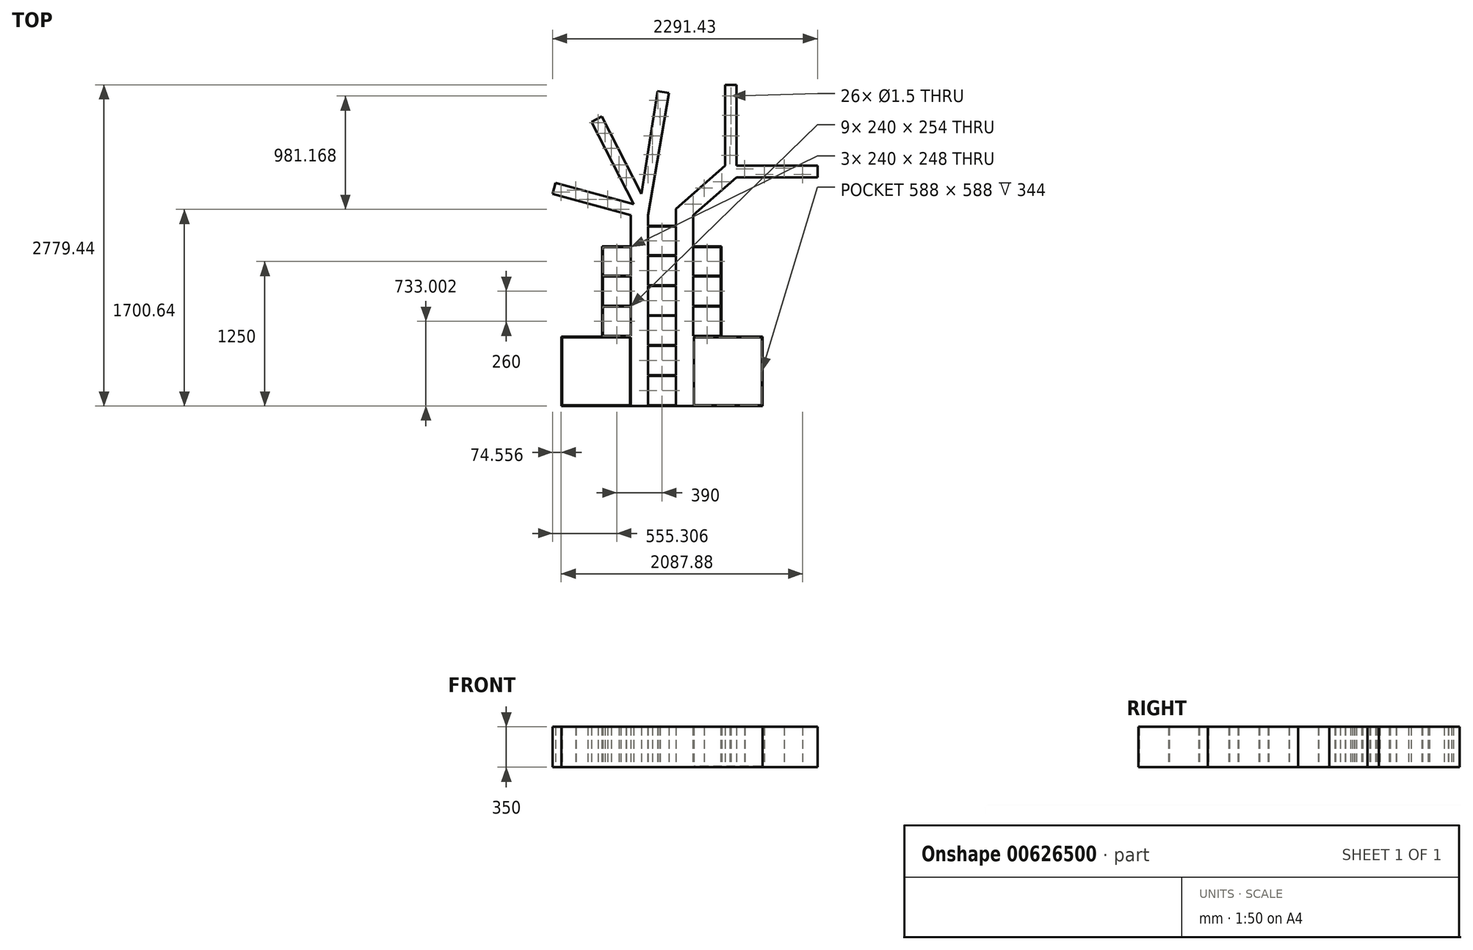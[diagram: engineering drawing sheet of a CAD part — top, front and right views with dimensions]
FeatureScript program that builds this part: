
annotation { "Feature Type Name" : "Feature", "Feature Type Description" : "" }
export const myFeature = defineFeature(function(context is Context, id is Id, definition is map)
    precondition{}
    {
        {
            var Q0;
            Q0=qCreatedBy(makeId("Top.planeOp"),FACE);
            var sketch = newSketch(context, id + "F0", { "sketchPlane" : qUnion([Q0])});
            skLineSegment(sketch, "E0", {"start": v(291.37, -157.74) * mm, "end": v(291.37, 1492.26) * mm});
            skLineSegment(sketch, "E1", {"start": v(831.37, 1492.26) * mm, "end": v(831.37, -157.74) * mm});
            skLineSegment(sketch, "E2", {"start": v(831.37, -157.74) * mm, "end": v(1431.37, -157.74) * mm});
            skLineSegment(sketch, "E3", {"start": v(1431.37, -157.74) * mm, "end": v(1431.37, 442.26) * mm});
            skLineSegment(sketch, "E4", {"start": v(1431.37, 442.26) * mm, "end": v(831.37, 442.26) * mm});
            skLineSegment(sketch, "E5", {"start": v(291.37, -157.74) * mm, "end": v(-308.63, -157.74) * mm});
            skLineSegment(sketch, "E6", {"start": v(-308.63, -157.74) * mm, "end": v(-308.63, 442.26) * mm});
            skLineSegment(sketch, "E7", {"start": v(-308.63, 442.26) * mm, "end": v(291.37, 442.26) * mm});
            skLineSegment(sketch, "E8", {"start": v(831.37, 1492.26) * mm, "end": v(1207.49, 1821.7) * mm});
            skLineSegment(sketch, "E9", {"start": v(1207.49, 1821.7) * mm, "end": v(1907.49, 1821.7) * mm});
            skLineSegment(sketch, "E10", {"start": v(1907.49, 1821.7) * mm, "end": v(1907.49, 1921.7) * mm});
            skLineSegment(sketch, "E11", {"start": v(1907.49, 1921.7) * mm, "end": v(1207.49, 1921.7) * mm});
            skLineSegment(sketch, "E12", {"start": v(1207.49, 1921.7) * mm, "end": v(1207.49, 2621.7) * mm});
            skLineSegment(sketch, "E13", {"start": v(1207.49, 2621.7) * mm, "end": v(1107.49, 2621.7) * mm});
            skLineSegment(sketch, "E14", {"start": v(1107.49, 2621.7) * mm, "end": v(1107.49, 1921.7) * mm});
            skLineSegment(sketch, "E15", {"start": v(291.37, -157.74) * mm, "end": v(441.37, -157.74) * mm});
            skLineSegment(sketch, "E16", {"start": v(441.37, -157.74) * mm, "end": v(681.37, -157.74) * mm});
            skLineSegment(sketch, "E17", {"start": v(681.37, -157.74) * mm, "end": v(831.37, -157.74) * mm});
            skLineSegment(sketch, "E18", {"start": v(681.37, -157.74) * mm, "end": v(681.37, 7.26) * mm});
            skLineSegment(sketch, "E19", {"start": v(681.37, 7.26) * mm, "end": v(681.37, 1492.26) * mm});
            skLineSegment(sketch, "E20", {"start": v(681.37, 1492.26) * mm, "end": v(831.37, 1492.26) * mm});
            skLineSegment(sketch, "E21", {"start": v(441.37, -157.74) * mm, "end": v(441.37, 1492.26) * mm});
            skLineSegment(sketch, "E22", {"start": v(441.37, 1492.26) * mm, "end": v(291.37, 1492.26) * mm});
            skLineSegment(sketch, "E23", {"start": v(1107.49, 1921.7) * mm, "end": v(681.37, 1548.47) * mm});
            skLineSegment(sketch, "E24", {"start": v(681.37, 1548.47) * mm, "end": v(681.37, 1492.26) * mm});
            skLineSegment(sketch, "E25", {"start": v(291.37, 1492.26) * mm, "end": v(-383.94, 1676.57) * mm});
            skLineSegment(sketch, "E26", {"start": v(-383.94, 1676.57) * mm, "end": v(-357.6, 1773.04) * mm});
            skLineSegment(sketch, "E27", {"start": v(-357.6, 1773.04) * mm, "end": v(317.7, 1588.73) * mm});
            skLineSegment(sketch, "E28", {"start": v(317.7, 1588.73) * mm, "end": v(-46.46, 2301.05) * mm});
            skLineSegment(sketch, "E29", {"start": v(-46.46, 2301.05) * mm, "end": v(42.58, 2346.57) * mm});
            skLineSegment(sketch, "E30", {"start": v(42.58, 2346.57) * mm, "end": v(385.1, 1676.57) * mm});
            skLineSegment(sketch, "E31", {"start": v(385.1, 1676.57) * mm, "end": v(523.43, 2565.87) * mm});
            skLineSegment(sketch, "E32", {"start": v(523.43, 2565.87) * mm, "end": v(622.24, 2550.5) * mm});
            skLineSegment(sketch, "E33", {"start": v(622.24, 2550.5) * mm, "end": v(441.37, 1492.26) * mm});
            skLineSegment(sketch, "E34", {"start": v(1071.37, 442.26) * mm, "end": v(831.37, 442.26) * mm});
            skLineSegment(sketch, "E35", {"start": v(1071.37, 442.26) * mm, "end": v(1071.37, 702.26) * mm});
            skLineSegment(sketch, "E36", {"start": v(1071.37, 702.26) * mm, "end": v(831.37, 702.26) * mm});
            skLineSegment(sketch, "E37", {"start": v(1071.37, 702.26) * mm, "end": v(1071.37, 962.26) * mm});
            skLineSegment(sketch, "E38", {"start": v(1071.37, 962.26) * mm, "end": v(831.37, 962.26) * mm});
            skLineSegment(sketch, "E39", {"start": v(1071.37, 962.26) * mm, "end": v(1071.37, 1222.26) * mm});
            skLineSegment(sketch, "E40", {"start": v(1071.37, 1222.26) * mm, "end": v(831.37, 1222.26) * mm});
            skLineSegment(sketch, "E41", {"start": v(51.37, 442.26) * mm, "end": v(291.37, 442.26) * mm});
            skLineSegment(sketch, "E42", {"start": v(51.37, 442.26) * mm, "end": v(51.37, 702.26) * mm});
            skLineSegment(sketch, "E43", {"start": v(51.37, 702.26) * mm, "end": v(291.37, 702.26) * mm});
            skLineSegment(sketch, "E44", {"start": v(51.37, 702.26) * mm, "end": v(51.37, 962.26) * mm});
            skLineSegment(sketch, "E45", {"start": v(291.37, 962.26) * mm, "end": v(51.37, 962.26) * mm});
            skLineSegment(sketch, "E46", {"start": v(51.37, 962.26) * mm, "end": v(51.37, 1222.26) * mm});
            skLineSegment(sketch, "E47", {"start": v(51.37, 1222.26) * mm, "end": v(291.37, 1222.26) * mm});
            skLineSegment(sketch, "E48", {"start": v(441.37, 102.26) * mm, "end": v(441.37, -157.74) * mm});
            skLineSegment(sketch, "E49", {"start": v(441.37, 102.26) * mm, "end": v(681.37, 102.26) * mm});
            skLineSegment(sketch, "E50", {"start": v(681.37, 102.26) * mm, "end": v(681.37, 362.26) * mm});
            skLineSegment(sketch, "E51", {"start": v(681.37, 362.26) * mm, "end": v(441.37, 362.26) * mm});
            skLineSegment(sketch, "E52", {"start": v(441.37, 362.26) * mm, "end": v(441.37, 622.26) * mm});
            skLineSegment(sketch, "E53", {"start": v(441.37, 622.26) * mm, "end": v(681.37, 622.26) * mm});
            skLineSegment(sketch, "E54", {"start": v(681.37, 622.26) * mm, "end": v(681.37, 882.26) * mm});
            skLineSegment(sketch, "E55", {"start": v(681.37, 882.26) * mm, "end": v(441.37, 882.26) * mm});
            skLineSegment(sketch, "E56", {"start": v(441.37, 882.26) * mm, "end": v(441.37, 1142.26) * mm});
            skLineSegment(sketch, "E57", {"start": v(441.37, 1142.26) * mm, "end": v(681.37, 1142.26) * mm});
            skLineSegment(sketch, "E58", {"start": v(681.37, 1142.26) * mm, "end": v(681.37, 1402.26) * mm});
            skLineSegment(sketch, "E59", {"start": v(681.37, 1402.26) * mm, "end": v(441.37, 1402.26) * mm});
            skLineSegment(sketch, "E60", {"start": v(441.37, 1148.26) * mm, "end": v(681.37, 1148.26) * mm});
            skLineSegment(sketch, "E61", {"start": v(441.37, 1396.26) * mm, "end": v(681.37, 1396.26) * mm});
            skLineSegment(sketch, "E62", {"start": v(441.37, 888.26) * mm, "end": v(681.37, 888.26) * mm});
            skLineSegment(sketch, "E63", {"start": v(441.37, 628.26) * mm, "end": v(681.37, 628.26) * mm});
            skLineSegment(sketch, "E64", {"start": v(441.37, 368.26) * mm, "end": v(681.37, 368.26) * mm});
            skLineSegment(sketch, "E65", {"start": v(441.37, 108.26) * mm, "end": v(681.37, 108.26) * mm});
            skLineSegment(sketch, "E66", {"start": v(441.37, -151.74) * mm, "end": v(681.37, -151.74) * mm});
            skLineSegment(sketch, "E67", {"start": v(1077.37, 1222.26) * mm, "end": v(1077.37, 442.26) * mm});
            skLineSegment(sketch, "E68", {"start": v(1071.37, 1222.26) * mm, "end": v(1077.37, 1222.26) * mm});
            skLineSegment(sketch, "E69", {"start": v(1071.37, 442.26) * mm, "end": v(1077.37, 442.26) * mm});
            skLineSegment(sketch, "E70", {"start": v(831.37, 1216.26) * mm, "end": v(1071.37, 1216.26) * mm});
            skLineSegment(sketch, "E71", {"start": v(831.37, 968.26) * mm, "end": v(1071.37, 968.26) * mm});
            skLineSegment(sketch, "E72", {"start": v(831.37, 708.26) * mm, "end": v(1071.37, 708.26) * mm});
            skLineSegment(sketch, "E73", {"start": v(831.37, 448.26) * mm, "end": v(1071.37, 448.26) * mm});
            skLineSegment(sketch, "E74", {"start": v(45.37, 442.26) * mm, "end": v(51.37, 442.26) * mm});
            skLineSegment(sketch, "E75", {"start": v(45.37, 442.26) * mm, "end": v(45.37, 1222.26) * mm});
            skLineSegment(sketch, "E76", {"start": v(51.37, 1216.26) * mm, "end": v(291.37, 1216.26) * mm});
            skLineSegment(sketch, "E77", {"start": v(51.37, 968.26) * mm, "end": v(291.37, 968.26) * mm});
            skLineSegment(sketch, "E78", {"start": v(51.37, 708.26) * mm, "end": v(291.37, 708.26) * mm});
            skLineSegment(sketch, "E79", {"start": v(51.37, 448.26) * mm, "end": v(291.37, 448.26) * mm});
            skLineSegment(sketch, "E80", {"start": v(45.37, 1222.26) * mm, "end": v(51.37, 1222.26) * mm});
            skCircle(sketch, "E81", {"center": v(-309.38, 1693.08) * mm, "radius": 0.75 * mm});
            skCircle(sketch, "E82", {"center": v(-182.87, 1710.9) * mm, "radius": 0.75 * mm});
            skCircle(sketch, "E83", {"center": v(-78.64, 1630.68) * mm, "radius": 0.75 * mm});
            skCircle(sketch, "E84", {"center": v(92.79, 1630.68) * mm, "radius": 0.75 * mm});
            skCircle(sketch, "E85", {"center": v(205.93, 1542.9) * mm, "radius": 0.75 * mm});
            skCircle(sketch, "E86", {"center": v(10.28, 2293.16) * mm, "radius": 0.75 * mm});
            skCircle(sketch, "E87", {"center": v(69.25, 2201.27) * mm, "radius": 0.75 * mm});
            skCircle(sketch, "E88", {"center": v(124.1, 2072.35) * mm, "radius": 0.75 * mm});
            skCircle(sketch, "E89", {"center": v(191.3, 1929.73) * mm, "radius": 0.75 * mm});
            skCircle(sketch, "E90", {"center": v(253.02, 1818.64) * mm, "radius": 0.75 * mm});
            skCircle(sketch, "E91", {"center": v(526.83, 2487.1) * mm, "radius": 0.75 * mm});
            skCircle(sketch, "E92", {"center": v(544.77, 2346.85) * mm, "radius": 0.75 * mm});
            skCircle(sketch, "E93", {"center": v(479.54, 2178.86) * mm, "radius": 0.75 * mm});
            skCircle(sketch, "E94", {"center": v(479.54, 2019.03) * mm, "radius": 0.75 * mm});
            skCircle(sketch, "E95", {"center": v(440.4, 1844.53) * mm, "radius": 0.75 * mm});
            skCircle(sketch, "E96", {"center": v(830.62, 1588.77) * mm, "radius": 0.75 * mm});
            skCircle(sketch, "E97", {"center": v(927.06, 1728.42) * mm, "radius": 0.75 * mm});
            skCircle(sketch, "E98", {"center": v(1078.12, 1782.72) * mm, "radius": 0.75 * mm});
            skCircle(sketch, "E99", {"center": v(1278.1, 1895.21) * mm, "radius": 0.75 * mm});
            skCircle(sketch, "E100", {"center": v(1448.78, 1844.79) * mm, "radius": 0.75 * mm});
            skCircle(sketch, "E101", {"center": v(1619.46, 1901.03) * mm, "radius": 0.75 * mm});
            skCircle(sketch, "E102", {"center": v(1778.5, 1846.73) * mm, "radius": 0.75 * mm});
            skCircle(sketch, "E103", {"center": v(1150.97, 2011.96) * mm, "radius": 0.75 * mm});
            skCircle(sketch, "E104", {"center": v(1157.5, 2178.86) * mm, "radius": 0.75 * mm});
            skCircle(sketch, "E105", {"center": v(1157.5, 2357.72) * mm, "radius": 0.75 * mm});
            skCircle(sketch, "E106", {"center": v(1157.5, 2524.07) * mm, "radius": 0.75 * mm});
            skLineSegment(sketch, "E107", {"start": v(837.37, -157.74) * mm, "end": v(837.37, 442.26) * mm});
            skLineSegment(sketch, "E108", {"start": v(837.37, 436.26) * mm, "end": v(1431.37, 436.26) * mm});
            skLineSegment(sketch, "E109", {"start": v(1425.37, 436.26) * mm, "end": v(1425.37, -157.74) * mm});
            skLineSegment(sketch, "E110", {"start": v(1425.37, -151.74) * mm, "end": v(837.37, -151.74) * mm});
            skLineSegment(sketch, "E111", {"start": v(-302.63, -157.74) * mm, "end": v(-302.63, 442.26) * mm});
            skLineSegment(sketch, "E112", {"start": v(-302.63, 436.26) * mm, "end": v(291.37, 436.26) * mm});
            skLineSegment(sketch, "E113", {"start": v(-302.63, -151.74) * mm, "end": v(291.37, -151.74) * mm});
            skLineSegment(sketch, "E114", {"start": v(285.37, -151.74) * mm, "end": v(285.37, 436.26) * mm});
            skSolve(sketch);
        }
        {
            var Q0;
            {var subQ0=sQuery(id+"F0.wireOp",EDGE,"E59");var subQ19=sQuery(id+"F0.wireOp",EDGE,"E75");var subQ31=sQuery(id+"F0.wireOp",EDGE,"E47");var subQ34=sQuery(id+"F0.wireOp",EDGE,"E8");var subQ44=sQuery(id+"F0.wireOp",EDGE,"E4");var subQ51=sQuery(id+"F0.wireOp",EDGE,"E67");var subQ58=sQuery(id+"F0.wireOp",EDGE,"E40");var subQ62=sQuery(id+"F0.wireOp",EDGE,"E22");var subQ63=makeQuery(id+"F0.imprint","IMPRINT",EDGE,{"derivedFrom":subQ62});var subQ86=sQuery(id+"F0.wireOp",EDGE,"E17");var subQ87=sQuery(id+"F0.wireOp",EDGE,"E16");var subQ91=sQuery(id+"F0.wireOp",EDGE,"E1");var subQ97=makeQuery(id+"F0.imprint","INTERSECT",VERTEX,{"derivedFrom":[subQ91,subQ44]});var subQ98=sQuery(id+"F0.wireOp",EDGE,"E2");var subQ104=sQuery(id+"F0.wireOp",EDGE,"E15");var subQ110=sQuery(id+"F0.wireOp",EDGE,"E110");var subQ112=sQuery(id+"F0.wireOp",EDGE,"E3");var subQ115=makeQuery(id+"F0.imprint","INTERSECT",VERTEX,{"derivedFrom":[subQ98,subQ112]});var subQ118=sQuery(id+"F0.wireOp",EDGE,"E0");var subQ136=sQuery(id+"F0.wireOp",EDGE,"E113");var subQ138=sQuery(id+"F0.wireOp",EDGE,"E112");var subQ139=makeQuery(id+"F0.imprint","INTERSECT",VERTEX,{"derivedFrom":[subQ118,subQ138]});var subQ145=makeQuery(id+"F0.imprint","IMPRINT",EDGE,{"disambiguationData":[TD([[subQ139,-1.0]])],"derivedFrom":subQ118});var subQ150=makeQuery(id+"F0.imprint","INTERSECT",VERTEX,{"derivedFrom":[subQ112,subQ44]});var subQ151=sQuery(id+"F0.wireOp",EDGE,"E111");var subQ152=makeQuery(id+"F0.imprint","INTERSECT",VERTEX,{"derivedFrom":[subQ151,subQ136]});var subQ156=makeQuery(id+"F0.imprint","IMPRINT",EDGE,{"disambiguationData":[TD([[subQ152,1.0]])],"derivedFrom":subQ151});var subQ158=sQuery(id+"F0.wireOp",EDGE,"E6");Q0=qUnion([makeQuery(id+"F0.imprint","IMPRINT",FACE,{"disambiguationData":[TD([[makeQuery(id+"F0.imprint","IMPRINT",EDGE,{"derivedFrom":subQ110}),1.0]])]}),makeQuery(id+"F0.imprint","IMPRINT",FACE,{"disambiguationData":[TD([[makeQuery(id+"F0.imprint","IMPRINT",EDGE,{"disambiguationData":[TD([[subQ97,1.0]])],"derivedFrom":subQ44}),1.0]])]}),makeQuery(id+"F0.imprint","IMPRINT",FACE,{"disambiguationData":[TD([[subQ145,1.0]])]}),makeQuery(id+"F0.imprint","IMPRINT",FACE,{"disambiguationData":[TD([[makeQuery(id+"F0.imprint","IMPRINT",EDGE,{"derivedFrom":subQ58}),1.0]])]}),makeQuery(id+"F0.imprint","IMPRINT",FACE,{"disambiguationData":[TD([[makeQuery(id+"F0.imprint","IMPRINT",EDGE,{"derivedFrom":subQ158}),-1.0]])]}),makeQuery(id+"F0.imprint","IMPRINT",FACE,{"disambiguationData":[TD([[subQ156,-1.0]])]}),makeQuery(id+"F0.imprint","IMPRINT",FACE,{"disambiguationData":[TD([[makeQuery(id+"F0.imprint","IMPRINT",EDGE,{"disambiguationData":[TD([[subQ150,1.0]])],"derivedFrom":subQ112}),1.0]])]}),makeQuery(id+"F0.imprint","IMPRINT",FACE,{"disambiguationData":[TD([[makeQuery(id+"F0.imprint","IMPRINT",EDGE,{"derivedFrom":subQ104}),1.0]])]}),makeQuery(id+"F0.imprint","IMPRINT",FACE,{"disambiguationData":[TD([[makeQuery(id+"F0.imprint","IMPRINT",EDGE,{"derivedFrom":subQ31}),-1.0]])]}),makeQuery(id+"F0.imprint","IMPRINT",FACE,{"disambiguationData":[TD([[makeQuery(id+"F0.imprint","IMPRINT",EDGE,{"disambiguationData":[TD([[subQ115,1.0]])],"derivedFrom":subQ98}),1.0]])]}),makeQuery(id+"F0.imprint","IMPRINT",FACE,{"disambiguationData":[TD([[makeQuery(id+"F0.imprint","IMPRINT",EDGE,{"derivedFrom":subQ87}),1.0]])]}),makeQuery(id+"F0.imprint","IMPRINT",FACE,{"disambiguationData":[TD([[makeQuery(id+"F0.imprint","IMPRINT",EDGE,{"derivedFrom":subQ86}),1.0]])]}),makeQuery(id+"F0.imprint","IMPRINT",FACE,{"disambiguationData":[TD([[subQ63,-1.0]])]}),makeQuery(id+"F0.imprint","IMPRINT",FACE,{"disambiguationData":[TD([[makeQuery(id+"F0.imprint","IMPRINT",EDGE,{"derivedFrom":subQ51}),-1.0]])]}),makeQuery(id+"F0.imprint","IMPRINT",FACE,{"disambiguationData":[TD([[makeQuery(id+"F0.imprint","IMPRINT",EDGE,{"derivedFrom":subQ34}),1.0]])]}),makeQuery(id+"F0.imprint","IMPRINT",FACE,{"disambiguationData":[TD([[makeQuery(id+"F0.imprint","IMPRINT",EDGE,{"derivedFrom":subQ19}),-1.0]])]}),makeQuery(id+"F0.imprint","IMPRINT",FACE,{"disambiguationData":[TD([[makeQuery(id+"F0.imprint","IMPRINT",EDGE,{"derivedFrom":subQ0}),1.0]])]})]);}
            var Q1;
            {var subQ0=sQuery(id+"F0.wireOp",EDGE,"E38");Q1=makeQuery(id+"F0.imprint","IMPRINT",FACE,{"disambiguationData":[TD([[makeQuery(id+"F0.imprint","IMPRINT",EDGE,{"derivedFrom":subQ0}),-1.0]])]});}
            var Q2;
            {var subQ0=sQuery(id+"F0.wireOp",EDGE,"E57");Q2=makeQuery(id+"F0.imprint","IMPRINT",FACE,{"disambiguationData":[TD([[makeQuery(id+"F0.imprint","IMPRINT",EDGE,{"derivedFrom":subQ0}),1.0]])]});}
            var Q3;
            {var subQ0=sQuery(id+"F0.wireOp",EDGE,"E55");Q3=makeQuery(id+"F0.imprint","IMPRINT",FACE,{"disambiguationData":[TD([[makeQuery(id+"F0.imprint","IMPRINT",EDGE,{"derivedFrom":subQ0}),-1.0]])]});}
            var Q4;
            {var subQ0=sQuery(id+"F0.wireOp",EDGE,"E53");Q4=makeQuery(id+"F0.imprint","IMPRINT",FACE,{"disambiguationData":[TD([[makeQuery(id+"F0.imprint","IMPRINT",EDGE,{"derivedFrom":subQ0}),1.0]])]});}
            var Q5;
            {var subQ0=sQuery(id+"F0.wireOp",EDGE,"E36");Q5=makeQuery(id+"F0.imprint","IMPRINT",FACE,{"disambiguationData":[TD([[makeQuery(id+"F0.imprint","IMPRINT",EDGE,{"derivedFrom":subQ0}),-1.0]])]});}
            var Q6;
            {var subQ0=sQuery(id+"F0.wireOp",EDGE,"E51");Q6=makeQuery(id+"F0.imprint","IMPRINT",FACE,{"disambiguationData":[TD([[makeQuery(id+"F0.imprint","IMPRINT",EDGE,{"derivedFrom":subQ0}),-1.0]])]});}
            var Q7;
            {var subQ3=sQuery(id+"F0.wireOp",EDGE,"E73");Q7=makeQuery(id+"F0.imprint","IMPRINT",FACE,{"disambiguationData":[TD([[makeQuery(id+"F0.imprint","IMPRINT",EDGE,{"derivedFrom":subQ3}),-1.0]])]});}
            var Q8;
            {var subQ2=sQuery(id+"F0.wireOp",EDGE,"E49");Q8=makeQuery(id+"F0.imprint","IMPRINT",FACE,{"disambiguationData":[TD([[makeQuery(id+"F0.imprint","IMPRINT",EDGE,{"derivedFrom":subQ2}),1.0]])]});}
            var Q9;
            {var subQ0=sQuery(id+"F0.wireOp",EDGE,"E43");Q9=makeQuery(id+"F0.imprint","IMPRINT",FACE,{"disambiguationData":[TD([[makeQuery(id+"F0.imprint","IMPRINT",EDGE,{"derivedFrom":subQ0}),1.0]])]});}
            var Q10;
            {var subQ0=sQuery(id+"F0.wireOp",EDGE,"E79");Q10=makeQuery(id+"F0.imprint","IMPRINT",FACE,{"disambiguationData":[TD([[makeQuery(id+"F0.imprint","IMPRINT",EDGE,{"derivedFrom":subQ0}),-1.0]])]});}
            var Q11;
            {var subQ0=sQuery(id+"F0.wireOp",EDGE,"E45");Q11=makeQuery(id+"F0.imprint","IMPRINT",FACE,{"disambiguationData":[TD([[makeQuery(id+"F0.imprint","IMPRINT",EDGE,{"derivedFrom":subQ0}),-1.0]])]});}
            extrude(context, id + "F1", {"entities" : qUnion([Q0, Q1, Q2, Q3, Q4, Q5, Q6, Q7, Q8, Q9, Q10, Q11]), "depth" : 350 * mm, "offsetDistance" : 25 * mm});
        }
        {
            var Q0;
            {var subQ0=sQuery(id+"F0.wireOp",EDGE,"E59");var subQ19=sQuery(id+"F0.wireOp",EDGE,"E75");var subQ31=sQuery(id+"F0.wireOp",EDGE,"E47");var subQ34=sQuery(id+"F0.wireOp",EDGE,"E8");var subQ44=sQuery(id+"F0.wireOp",EDGE,"E4");var subQ51=sQuery(id+"F0.wireOp",EDGE,"E67");var subQ58=sQuery(id+"F0.wireOp",EDGE,"E40");var subQ62=sQuery(id+"F0.wireOp",EDGE,"E22");var subQ63=makeQuery(id+"F0.imprint","IMPRINT",EDGE,{"derivedFrom":subQ62});var subQ86=sQuery(id+"F0.wireOp",EDGE,"E17");var subQ87=sQuery(id+"F0.wireOp",EDGE,"E16");var subQ91=sQuery(id+"F0.wireOp",EDGE,"E1");var subQ97=makeQuery(id+"F0.imprint","INTERSECT",VERTEX,{"derivedFrom":[subQ91,subQ44]});var subQ98=sQuery(id+"F0.wireOp",EDGE,"E2");var subQ104=sQuery(id+"F0.wireOp",EDGE,"E15");var subQ110=sQuery(id+"F0.wireOp",EDGE,"E110");var subQ112=sQuery(id+"F0.wireOp",EDGE,"E3");var subQ115=makeQuery(id+"F0.imprint","INTERSECT",VERTEX,{"derivedFrom":[subQ98,subQ112]});var subQ118=sQuery(id+"F0.wireOp",EDGE,"E0");var subQ136=sQuery(id+"F0.wireOp",EDGE,"E113");var subQ138=sQuery(id+"F0.wireOp",EDGE,"E112");var subQ139=makeQuery(id+"F0.imprint","INTERSECT",VERTEX,{"derivedFrom":[subQ118,subQ138]});var subQ145=makeQuery(id+"F0.imprint","IMPRINT",EDGE,{"disambiguationData":[TD([[subQ139,-1.0]])],"derivedFrom":subQ118});var subQ150=makeQuery(id+"F0.imprint","INTERSECT",VERTEX,{"derivedFrom":[subQ112,subQ44]});var subQ151=sQuery(id+"F0.wireOp",EDGE,"E111");var subQ152=makeQuery(id+"F0.imprint","INTERSECT",VERTEX,{"derivedFrom":[subQ151,subQ136]});var subQ156=makeQuery(id+"F0.imprint","IMPRINT",EDGE,{"disambiguationData":[TD([[subQ152,1.0]])],"derivedFrom":subQ151});var subQ158=sQuery(id+"F0.wireOp",EDGE,"E6");Q0=qUnion([makeQuery(id+"F0.imprint","IMPRINT",FACE,{"disambiguationData":[TD([[makeQuery(id+"F0.imprint","IMPRINT",EDGE,{"derivedFrom":subQ110}),1.0]])]}),makeQuery(id+"F0.imprint","IMPRINT",FACE,{"disambiguationData":[TD([[makeQuery(id+"F0.imprint","IMPRINT",EDGE,{"disambiguationData":[TD([[subQ97,1.0]])],"derivedFrom":subQ44}),1.0]])]}),makeQuery(id+"F0.imprint","IMPRINT",FACE,{"disambiguationData":[TD([[subQ145,1.0]])]}),makeQuery(id+"F0.imprint","IMPRINT",FACE,{"disambiguationData":[TD([[makeQuery(id+"F0.imprint","IMPRINT",EDGE,{"derivedFrom":subQ58}),1.0]])]}),makeQuery(id+"F0.imprint","IMPRINT",FACE,{"disambiguationData":[TD([[makeQuery(id+"F0.imprint","IMPRINT",EDGE,{"derivedFrom":subQ158}),-1.0]])]}),makeQuery(id+"F0.imprint","IMPRINT",FACE,{"disambiguationData":[TD([[subQ156,-1.0]])]}),makeQuery(id+"F0.imprint","IMPRINT",FACE,{"disambiguationData":[TD([[makeQuery(id+"F0.imprint","IMPRINT",EDGE,{"disambiguationData":[TD([[subQ150,1.0]])],"derivedFrom":subQ112}),1.0]])]}),makeQuery(id+"F0.imprint","IMPRINT",FACE,{"disambiguationData":[TD([[makeQuery(id+"F0.imprint","IMPRINT",EDGE,{"derivedFrom":subQ104}),1.0]])]}),makeQuery(id+"F0.imprint","IMPRINT",FACE,{"disambiguationData":[TD([[makeQuery(id+"F0.imprint","IMPRINT",EDGE,{"derivedFrom":subQ31}),-1.0]])]}),makeQuery(id+"F0.imprint","IMPRINT",FACE,{"disambiguationData":[TD([[makeQuery(id+"F0.imprint","IMPRINT",EDGE,{"disambiguationData":[TD([[subQ115,1.0]])],"derivedFrom":subQ98}),1.0]])]}),makeQuery(id+"F0.imprint","IMPRINT",FACE,{"disambiguationData":[TD([[makeQuery(id+"F0.imprint","IMPRINT",EDGE,{"derivedFrom":subQ87}),1.0]])]}),makeQuery(id+"F0.imprint","IMPRINT",FACE,{"disambiguationData":[TD([[makeQuery(id+"F0.imprint","IMPRINT",EDGE,{"derivedFrom":subQ86}),1.0]])]}),makeQuery(id+"F0.imprint","IMPRINT",FACE,{"disambiguationData":[TD([[subQ63,-1.0]])]}),makeQuery(id+"F0.imprint","IMPRINT",FACE,{"disambiguationData":[TD([[makeQuery(id+"F0.imprint","IMPRINT",EDGE,{"derivedFrom":subQ51}),-1.0]])]}),makeQuery(id+"F0.imprint","IMPRINT",FACE,{"disambiguationData":[TD([[makeQuery(id+"F0.imprint","IMPRINT",EDGE,{"derivedFrom":subQ34}),1.0]])]}),makeQuery(id+"F0.imprint","IMPRINT",FACE,{"disambiguationData":[TD([[makeQuery(id+"F0.imprint","IMPRINT",EDGE,{"derivedFrom":subQ19}),-1.0]])]}),makeQuery(id+"F0.imprint","IMPRINT",FACE,{"disambiguationData":[TD([[makeQuery(id+"F0.imprint","IMPRINT",EDGE,{"derivedFrom":subQ0}),1.0]])]})]);}
            var Q1;
            {var subQ5=sQuery(id+"F0.wireOp",EDGE,"E114");Q1=makeQuery(id+"F0.imprint","IMPRINT",FACE,{"disambiguationData":[TD([[makeQuery(id+"F0.imprint","IMPRINT",EDGE,{"derivedFrom":subQ5}),1.0]])]});}
            var Q2;
            {var subQ0=sQuery(id+"F0.wireOp",EDGE,"E110");Q2=makeQuery(id+"F0.imprint","IMPRINT",FACE,{"disambiguationData":[TD([[makeQuery(id+"F0.imprint","IMPRINT",EDGE,{"derivedFrom":subQ0}),-1.0]])]});}
            extrude(context, id + "F2", {"entities" : qUnion([Q0, Q1, Q2]), "operationType" : NewBodyOperationType.ADD, "depth" : 6 * mm, "offsetDistance" : 25 * mm});
        }
    });
